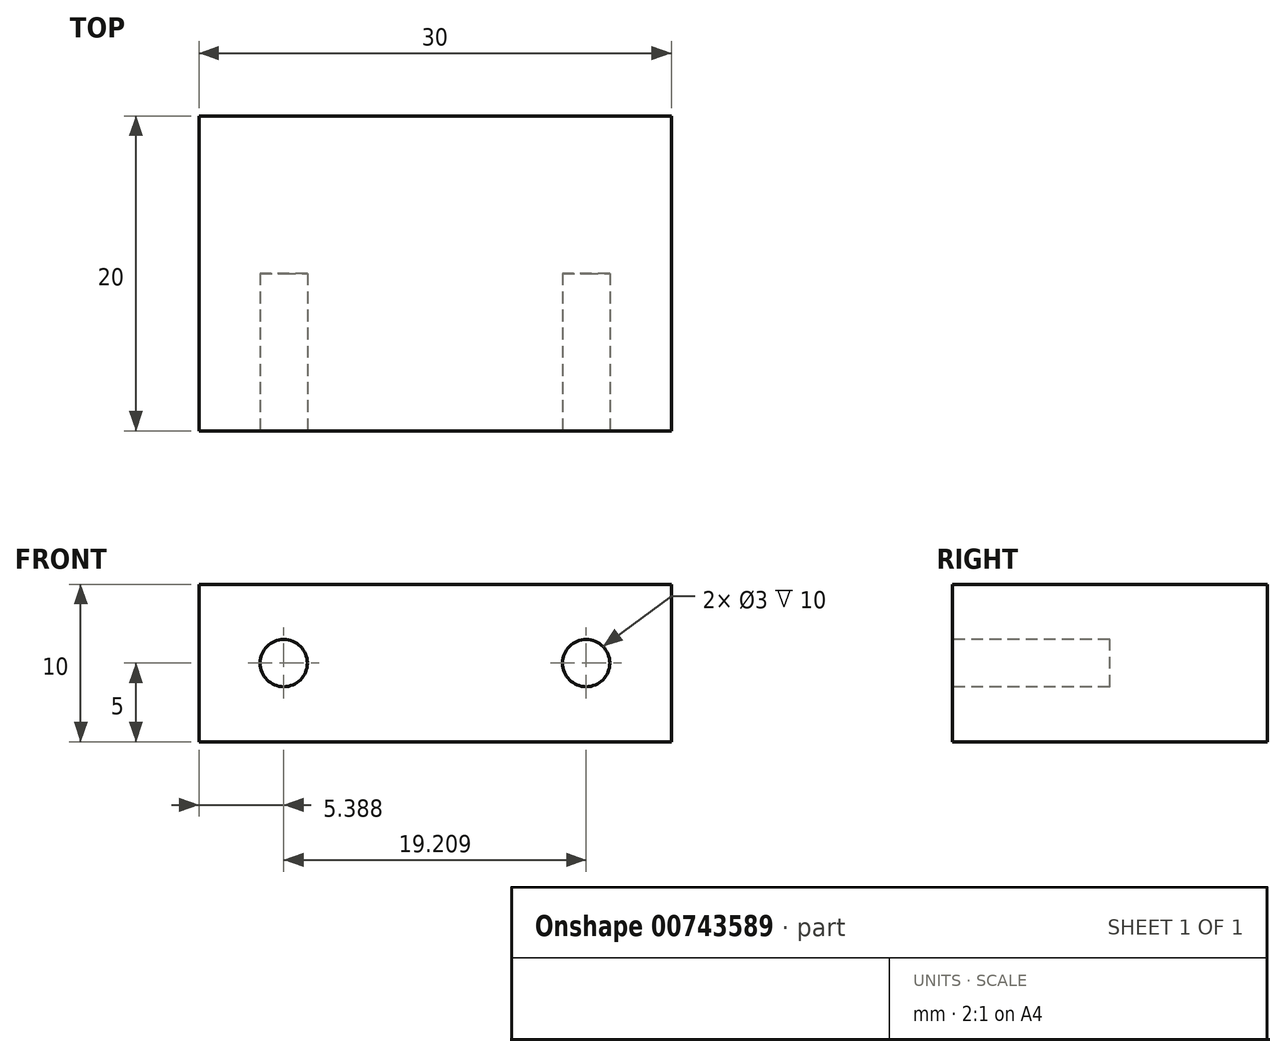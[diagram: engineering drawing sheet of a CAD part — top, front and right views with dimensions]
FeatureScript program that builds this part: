
annotation { "Feature Type Name" : "Feature", "Feature Type Description" : "" }
export const myFeature = defineFeature(function(context is Context, id is Id, definition is map)
    precondition{}
    {
        {
            var Q0;
            Q0=qCreatedBy(makeId("Front.planeOp"),FACE);
            var sketch = newSketch(context, id + "F0", { "sketchPlane" : qUnion([Q0])});
            skLineSegment(sketch, "E0.bottom", {"start": v(15, 5) * mm, "end": v(-15, 5) * mm});
            skLineSegment(sketch, "E0.top", {"start": v(15, -5) * mm, "end": v(-15, -5) * mm});
            skLineSegment(sketch, "E0.left", {"start": v(15, 5) * mm, "end": v(15, -5) * mm});
            skLineSegment(sketch, "E0.right", {"start": v(-15, 5) * mm, "end": v(-15, -5) * mm});
            skPoint(sketch, "E0.middle", {"position": v(0, 0) * mm});
            skSolve(sketch);
        }
        {
            var Q0;
            Q0=makeQuery(id+"F0.imprint","IMPRINT",FACE,{"disambiguationData":[TD([[makeQuery(id+"F0.imprint","IMPRINT",EDGE,{"derivedFrom":sQuery(id+"F0.wireOp",EDGE,"E0.bottom")}),1.0]])]});
            extrude(context, id + "F1", {"entities" : qUnion([Q0]), "depth" : 20 * mm, "offsetDistance" : 25.4 * mm});
        }
        {
            var Q0;
            Q0=makeQuery(id+"F1.opExtrude","CAP_FACE",FACE,{"disambiguationData":[OSD([sQuery(id+"F0.wireOp",EDGE,"E0.bottom"),sQuery(id+"F0.wireOp",EDGE,"E0.top"),sQuery(id+"F0.wireOp",EDGE,"E0.left"),sQuery(id+"F0.wireOp",EDGE,"E0.right")])],"isStart":false});
            var sketch = newSketch(context, id + "F2", { "sketchPlane" : qUnion([Q0])});
            skCircle(sketch, "E1", {"center": v(9.6, 0) * mm, "radius": 1.5 * mm});
            skSolve(sketch);
        }
        {
            var Q0;
            Q0=makeQuery(id+"F2.imprint","IMPRINT",FACE,{"disambiguationData":[TD([[makeQuery(id+"F2.imprint","IMPRINT",EDGE,{"derivedFrom":sQuery(id+"F2.wireOp",EDGE,"E1")}),-1.0]])]});
            var sketch = newSketch(context, id + "F3", { "sketchPlane" : qUnion([Q0])});
            skCircle(sketch, "E2", {"center": v(-9.61, 0) * mm, "radius": 1.5 * mm});
            skSolve(sketch);
        }
        {
            var Q0;
            Q0=makeQuery(id+"F3.imprint","IMPRINT",FACE,{"disambiguationData":[TD([[makeQuery(id+"F3.imprint","IMPRINT",EDGE,{"derivedFrom":makeQuery(id+"F2.imprint","IMPRINT",EDGE,{"derivedFrom":sQuery(id+"F2.wireOp",EDGE,"E1")})}),1.0]])]});
            extrude(context, id + "F4", {"entities" : qUnion([Q0]), "operationType" : NewBodyOperationType.REMOVE, "oppositeDirection" : true, "depth" : 10 * mm, "offsetDistance" : 25.4 * mm});
        }
        {
            var Q0;
            Q0=makeQuery(id+"F3.imprint","IMPRINT",FACE,{"disambiguationData":[TD([[makeQuery(id+"F3.imprint","IMPRINT",EDGE,{"derivedFrom":sQuery(id+"F3.wireOp",EDGE,"E2")}),1.0]])]});
            extrude(context, id + "F5", {"entities" : qUnion([Q0]), "operationType" : NewBodyOperationType.REMOVE, "oppositeDirection" : true, "depth" : 10 * mm, "offsetDistance" : 25.4 * mm});
        }
    });
